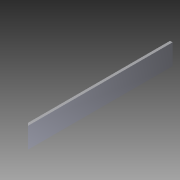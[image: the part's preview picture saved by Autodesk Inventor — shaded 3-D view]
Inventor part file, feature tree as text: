
AUTODESK INVENTOR PART (.ipt)
format: ipt  version: 2012 (Build 160160000, 160)  size: 94,208 bytes
history: native  units: in
note: dims shown in document units (in); Inventor stores cm internally (conversion verified against a paired STEP export)
features: extrude x2, sketch x2, mirror x1
ambient origin geometry x8: Origin, YZ Plane, XZ Plane, XY Plane, X Axis, Y Axis, Z Axis, Center Point
bodies: Solid1 (feature_tree)
feature tree (5):
  extrude  "Extrusion1"  Depth=1.0in
  extrude  "Extrusion2"  Depth=0.125in
  mirror  "Mirror1"
  sketch  "Sketch1"  dims[d0=1.0in d1=1.0in]
  sketch  "Sketch2"  dims[d2=0.125in d3=0.125in d4=7.0in d5=0.0in d6=45.0deg d7=1.625in d8=3.0in d9=0.25in d10=0.5in d11=7.0in d12=0.0in]
